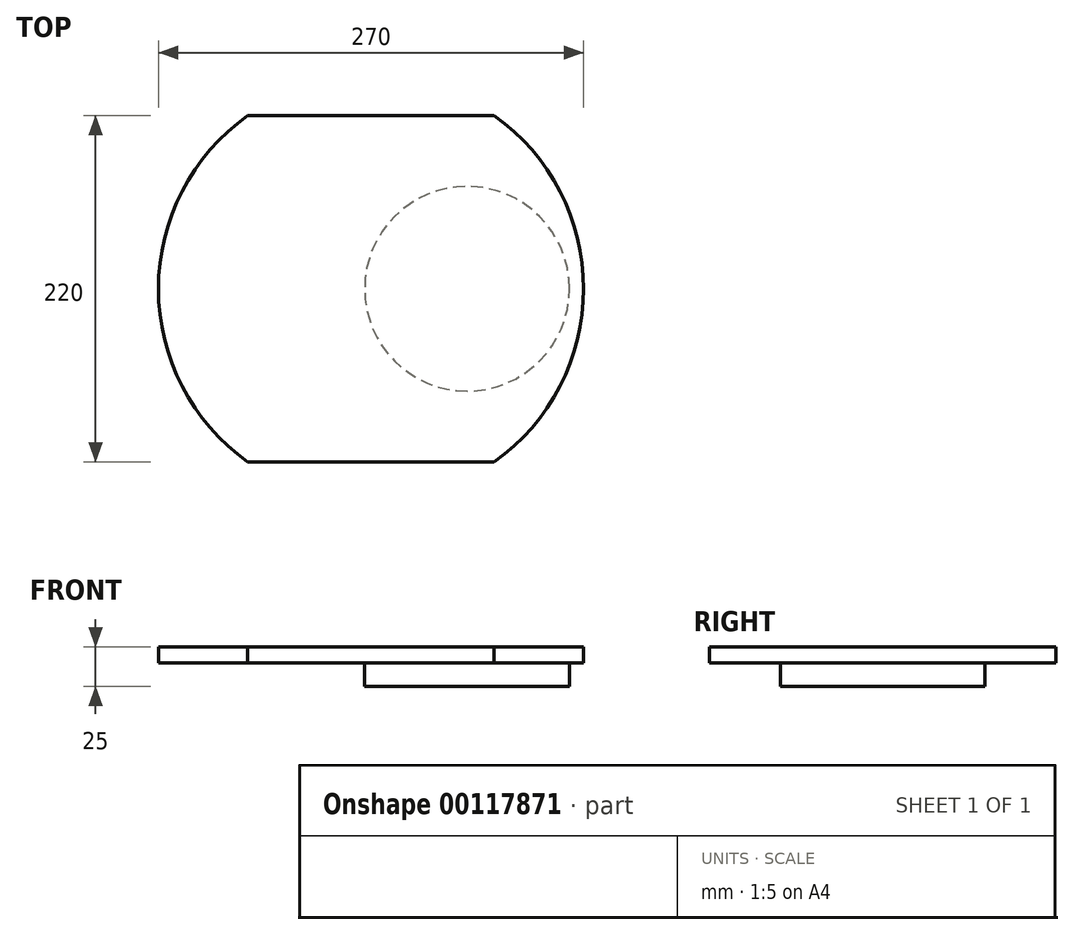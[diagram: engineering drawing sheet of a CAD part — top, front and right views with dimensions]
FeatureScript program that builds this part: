
annotation { "Feature Type Name" : "Feature", "Feature Type Description" : "" }
export const myFeature = defineFeature(function(context is Context, id is Id, definition is map)
    precondition{}
    {
        {
            var Q0;
            Q0=qCreatedBy(makeId("Top.planeOp"),FACE);
            var sketch = newSketch(context, id + "F0", { "sketchPlane" : qUnion([Q0])});
            skLineSegment(sketch, "E0", {"start": v(-78.26, -110) * mm, "end": v(78.26, -110) * mm});
            skArc(sketch, "E1", {"start": v(-78.26, 110) * mm, "mid": v(-135, 0) * mm, "end": v(-78.26, -110) * mm});
            skArc(sketch, "E2", {"start": v(78.26, -110) * mm, "mid": v(135, 0) * mm, "end": v(78.26, 110) * mm});
            skLineSegment(sketch, "E3", {"start": v(-78.26, 110) * mm, "end": v(78.26, 110) * mm});
            skSolve(sketch);
        }
        {
            var Q0;
            Q0=makeQuery(id+"F0.imprint","IMPRINT",FACE,{"disambiguationData":[TD([[makeQuery(id+"F0.imprint","IMPRINT",EDGE,{"derivedFrom":sQuery(id+"F0.wireOp",EDGE,"E0")}),1.0]])]});
            extrude(context, id + "F1", {"entities" : qUnion([Q0]), "depth" : 10 * mm});
        }
        {
            var Q0;
            Q0=makeQuery(id+"F1.opExtrude","CAP_FACE",FACE,{"disambiguationData":[OSD([sQuery(id+"F0.wireOp",EDGE,"E0"),sQuery(id+"F0.wireOp",EDGE,"E1"),sQuery(id+"F0.wireOp",EDGE,"E2"),sQuery(id+"F0.wireOp",EDGE,"E3")])],"isStart":false});
            var sketch = newSketch(context, id + "F2", { "sketchPlane" : qUnion([Q0])});
            skArc(sketch, "E4", {"start": v(-69.28, 110) * mm, "mid": v(-130, 0) * mm, "end": v(-69.28, -110) * mm});
            skArc(sketch, "E5", {"start": v(69.28, -110) * mm, "mid": v(130, 0) * mm, "end": v(69.28, 110) * mm});
            skArc(sketch, "E6", {"start": v(-61.45, 110) * mm, "mid": v(-126, 0) * mm, "end": v(-61.45, -110) * mm});
            skArc(sketch, "E7", {"start": v(61.45, -110) * mm, "mid": v(126, 0) * mm, "end": v(61.45, 110) * mm});
            skLineSegment(sketch, "E8", {"start": v(-69.28, 110) * mm, "end": v(-61.45, 110) * mm});
            skLineSegment(sketch, "E9", {"start": v(61.45, 110) * mm, "end": v(69.28, 110) * mm});
            skLineSegment(sketch, "E10", {"start": v(-69.28, -110) * mm, "end": v(-61.45, -110) * mm});
            skLineSegment(sketch, "E11", {"start": v(61.45, -110) * mm, "end": v(69.28, -110) * mm});
            skSolve(sketch);
        }
        {
            var Q0;
            Q0=makeQuery(id+"F2.imprint","IMPRINT",FACE,{"disambiguationData":[TD([[makeQuery(id+"F2.imprint","IMPRINT",EDGE,{"derivedFrom":sQuery(id+"F2.wireOp",EDGE,"E4")}),1.0]])]});
            var Q1;
            Q1=makeQuery(id+"F2.imprint","IMPRINT",FACE,{"disambiguationData":[TD([[makeQuery(id+"F2.imprint","IMPRINT",EDGE,{"derivedFrom":sQuery(id+"F2.wireOp",EDGE,"E5")}),1.0]])]});
            extrude(context, id + "F3", {"entities" : qUnion([Q0, Q1]), "operationType" : NewBodyOperationType.REMOVE, "oppositeDirection" : true, "depth" : 4 * mm});
        }
        {
            var Q0;
            Q0=makeQuery(id+"F1.opExtrude","CAP_FACE",FACE,{"disambiguationData":[OSD([sQuery(id+"F0.wireOp",EDGE,"E0"),sQuery(id+"F0.wireOp",EDGE,"E1"),sQuery(id+"F0.wireOp",EDGE,"E2"),sQuery(id+"F0.wireOp",EDGE,"E3")])],"isStart":true});
            var sketch = newSketch(context, id + "F4", { "sketchPlane" : qUnion([Q0])});
            skSolve(sketch);
        }
        {
            var Q0;
            Q0=makeQuery(id+"F3.boolean.opBoolean","COPY",FACE,{"derivedFrom":makeQuery(id+"F3.opExtrude","CAP_FACE",FACE,{"disambiguationData":[OSD([sQuery(id+"F2.wireOp",EDGE,"E4"),sQuery(id+"F2.wireOp",EDGE,"E6"),sQuery(id+"F2.wireOp",EDGE,"E8"),sQuery(id+"F2.wireOp",EDGE,"E10")])],"isStart":false})});
            var Q1;
            Q1=makeQuery(id+"F3.boolean.opBoolean","COPY",FACE,{"derivedFrom":makeQuery(id+"F3.opExtrude","CAP_FACE",FACE,{"disambiguationData":[OSD([sQuery(id+"F2.wireOp",EDGE,"E5"),sQuery(id+"F2.wireOp",EDGE,"E7"),sQuery(id+"F2.wireOp",EDGE,"E9"),sQuery(id+"F2.wireOp",EDGE,"E11")])],"isStart":false})});
            extrude(context, id + "F5", {"entities" : qUnion([Q0, Q1]), "operationType" : NewBodyOperationType.ADD, "depth" : 50 * mm});
        }
        {
            var Q0;
            Q0=makeQuery(id+"F4.imprint","IMPRINT",FACE,{"disambiguationData":[TD([[makeQuery(id+"F4.imprint","IMPRINT",EDGE,{"derivedFrom":makeQuery(id+"F1.opExtrude","CAP_EDGE",EDGE,{"disambiguationData":[OSD([sQuery(id+"F0.wireOp",EDGE,"E0")])],"isStart":true})}),-1.0]])]});
            var sketch = newSketch(context, id + "F6", { "sketchPlane" : qUnion([Q0])});
            skLineSegment(sketch, "E12", {"start": v(135, 0) * mm, "end": v(61, 0) * mm});
            skCircle(sketch, "E13", {"center": v(61, 0) * mm, "radius": 65 * mm});
            skSolve(sketch);
        }
        {
            var Q0;
            Q0=makeQuery(id+"F6.imprint","IMPRINT",FACE,{"disambiguationData":[TD([[makeQuery(id+"F6.imprint","IMPRINT",EDGE,{"derivedFrom":sQuery(id+"F6.wireOp",EDGE,"E13")}),1.0]])]});
            extrude(context, id + "F7", {"entities" : qUnion([Q0]), "operationType" : NewBodyOperationType.ADD, "depth" : 15 * mm});
        }
        {
            var Q0;
            Q0=makeQuery(id+"F5.opExtrude","CAP_FACE",FACE,{"disambiguationData":[OSD([sQuery(id+"F2.wireOp",EDGE,"E4"),sQuery(id+"F2.wireOp",EDGE,"E6"),sQuery(id+"F2.wireOp",EDGE,"E8"),sQuery(id+"F2.wireOp",EDGE,"E10")])],"isStart":false});
            var Q1;
            Q1=makeQuery(id+"F5.opExtrude","CAP_FACE",FACE,{"disambiguationData":[OSD([sQuery(id+"F2.wireOp",EDGE,"E5"),sQuery(id+"F2.wireOp",EDGE,"E7"),sQuery(id+"F2.wireOp",EDGE,"E9"),sQuery(id+"F2.wireOp",EDGE,"E11")])],"isStart":false});
            extrude(context, id + "F8", {"entities" : qUnion([Q0, Q1]), "operationType" : NewBodyOperationType.REMOVE, "oppositeDirection" : true, "depth" : 50 * mm});
        }
        {
            var Q0;
            Q0=makeQuery(id+"F8.boolean.opBoolean","COPY",FACE,{"derivedFrom":makeQuery(id+"F8.opExtrude","CAP_FACE",FACE,{"disambiguationData":[OSD([sQuery(id+"F2.wireOp",EDGE,"E4"),sQuery(id+"F2.wireOp",EDGE,"E6"),sQuery(id+"F2.wireOp",EDGE,"E8"),sQuery(id+"F2.wireOp",EDGE,"E10")])],"isStart":false})});
            var Q1;
            Q1=makeQuery(id+"F8.boolean.opBoolean","COPY",FACE,{"derivedFrom":makeQuery(id+"F8.opExtrude","CAP_FACE",FACE,{"disambiguationData":[OSD([sQuery(id+"F2.wireOp",EDGE,"E5"),sQuery(id+"F2.wireOp",EDGE,"E7"),sQuery(id+"F2.wireOp",EDGE,"E9"),sQuery(id+"F2.wireOp",EDGE,"E11")])],"isStart":false})});
            extrude(context, id + "F9", {"entities" : qUnion([Q0, Q1]), "operationType" : NewBodyOperationType.ADD, "depth" : 4 * mm});
        }
    });
